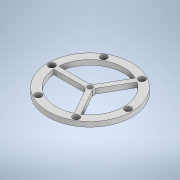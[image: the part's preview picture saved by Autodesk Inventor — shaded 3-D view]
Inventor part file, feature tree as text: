
AUTODESK INVENTOR PART (.ipt)
format: ipt  version: 2021 (Build 250183000, 183)  size: 148,992 bytes
history: native  units: mm
features: extrude x1, sketch x1
ambient origin geometry x8: Origin, YZ Plane, XZ Plane, XY Plane, X Axis, Y Axis, Z Axis, Center Point
bodies: Body1 (feature_tree)
feature tree (2):
  extrude  "Extrusion2"  Depth=6.0mm
  sketch  "Sketch1"  dims[d0=102.9mm d1=82.9mm d2=6.0mm d3=10.0mm d5=30.0mm d7=360.0deg d9=6.0mm d10=30.0mm d12=360.0deg d16=8.0mm d17=46.5mm d18=60.0mm d20=360.0deg d22=6.0mm d23=0.0mm]
